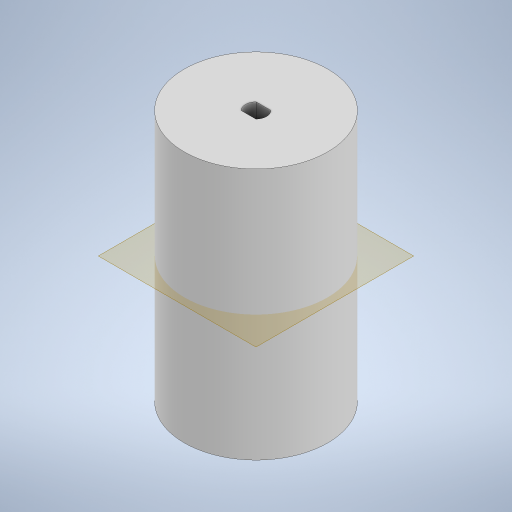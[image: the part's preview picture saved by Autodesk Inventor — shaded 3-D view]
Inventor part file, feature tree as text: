
AUTODESK INVENTOR PART (.ipt)
format: ipt  version: 2024 (Build 280153020, 153B)  size: 375,296 bytes
history: native  units: in
note: dims shown in document units (in); Inventor stores cm internally (conversion verified against a paired STEP export)
features: sketch x8, extrude x4, plane x4, loft x1, mirror x1
ambient origin geometry x8: Origin, YZ Plane, XZ Plane, XY Plane, X Axis, Y Axis, Z Axis, Center Point
bodies: Solid1 (feature_tree)
feature tree (18):
  extrude  "Extrusion1"  Depth=2.6378in TaperAngle=0.0deg
  extrude  "Extrusion2"  Depth=0.2756in TaperAngle=0.0deg
  plane  "Work Plane1"
  plane  "Work Plane2"
  sketch  "Sketch4"  dims[d6=-0.5906in d7=1.1in]
  sketch  "Sketch5"  dims[d8=0.1969in d10=-0.1969in]
  plane  "Work Plane3"
  plane  "Work Plane4"
  loft  "Loft1"
  mirror  "Mirror1"
  extrude  "Extrusion3"  [1 undecoded]
  extrude  "Extrusion4"  Depth=1.1in
  sketch  "Sketch1"  dims[d0=1.5in d1=2.6378in d2=0.0in]
  sketch  "Sketch2"  dims[d3=0.8681in d4=0.2756in d5=0.0in]
  sketch  "Sketch8"  dims[d11=0.748in d12=1.1in]
  sketch  "Sketch9"  dims[d13=0.0in d14=90.0deg]
  sketch  "Sketch10"  dims[d15=0.0in d16=90.0deg]
  sketch  "Sketch12"  dims[d17=0.0in d18=90.0deg d19=0.0in d20=90.0deg d21=0.5in d22=0.0in d23=0.2205in d24=0.0787in d25=0.0787in d26=0.3937in d27=0.0in]
note: 1 required parameter value undecoded (feature->parameter linkage not recoverable at this tier; creation-order binding heuristic only, values carry confidence <= 0.55)
